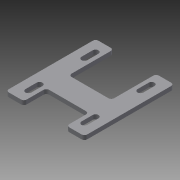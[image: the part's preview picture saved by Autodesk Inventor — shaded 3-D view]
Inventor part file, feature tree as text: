
AUTODESK INVENTOR PART (.ipt)
format: ipt  version: 2013 (Build 170138000, 138)  size: 127,488 bytes
history: native  units: in
note: dims shown in document units (in); Inventor stores cm internally (conversion verified against a paired STEP export)
features: extrude x1, fillet x1, mirror x1, sketch x1
ambient origin geometry x8: Origin, YZ Plane, XZ Plane, XY Plane, X Axis, Y Axis, Z Axis, Center Point
bodies: Solid1 (feature_tree)
feature tree (4):
  extrude  "Extrusion1"  Depth=0.1875in TaperAngle=0.0deg
  fillet  "Fillet1"  Radius=1.75in
  mirror  "Mirror2"
  sketch  "Sketch1"  dims[d1=4.0in d6=0.1875in d7=0.0in d8=1.75in d11=0.26in d14=0.5in d15=0.5in d18=0.5in d19=0.8in d20=0.125in d21=1.25in d23=1.0in d24=2.0in d25=2.5in d26=0.26in]
